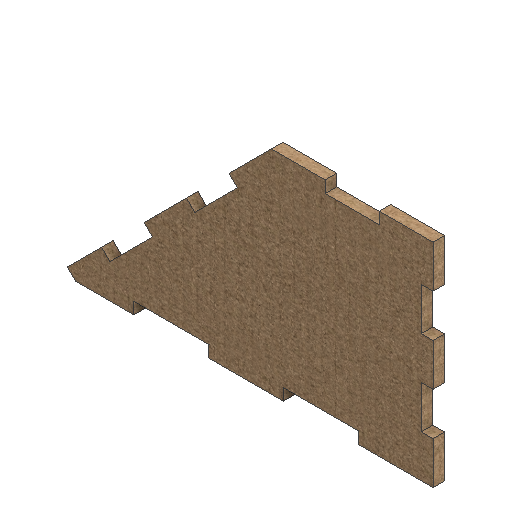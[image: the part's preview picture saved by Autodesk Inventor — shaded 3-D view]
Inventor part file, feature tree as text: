
AUTODESK INVENTOR PART (.ipt)
format: ipt  version: 2025.2 (Build 292293000, 293)  size: 353,792 bytes
history: native  units: mm
features: extrude x4, sketch x4, projected_geometry x2
ambient origin geometry x8: Origin, YZ Plane, XZ Plane, XY Plane, X Axis, Y Axis, Z Axis, Center Point
bodies: Solid1 (feature_tree)
feature tree (10):
  extrude  "Extrusion1"  Depth=130.0mm
  extrude  "Extrusion2"  Depth=92.0mm
  extrude  "Extrusion3"  Depth=26.1mm
  extrude  "Extrusion4"  Depth=5.0mm TaperAngle=0.0deg
  sketch  "Sketch1"  dims[d1=70.0mm d2=130.0mm]
  sketch  "Sketch2"  dims[d4=5.0mm d5=0.0mm d7=92.0mm]
  sketch  "Sketch3"  dims[d8=130.0mm d9=26.1mm]
  projected_geometry  "Projected Loop1"
  sketch  "Sketch4"  dims[d10=25.9mm d11=10.0mm d12=0.0mm d13=5.1mm d14=70.0mm d15=92.0mm d16=161.8477mm d17=32.26954mm d18=32.46954mm d19=18.3mm d20=18.5mm d21=23.433333mm d22=5.0mm d23=5.0mm d24=0.0mm d27=5.0mm d28=0.0mm d29=0.0mm d25=0.872665mm]
  projected_geometry  "Projected Loop2"
